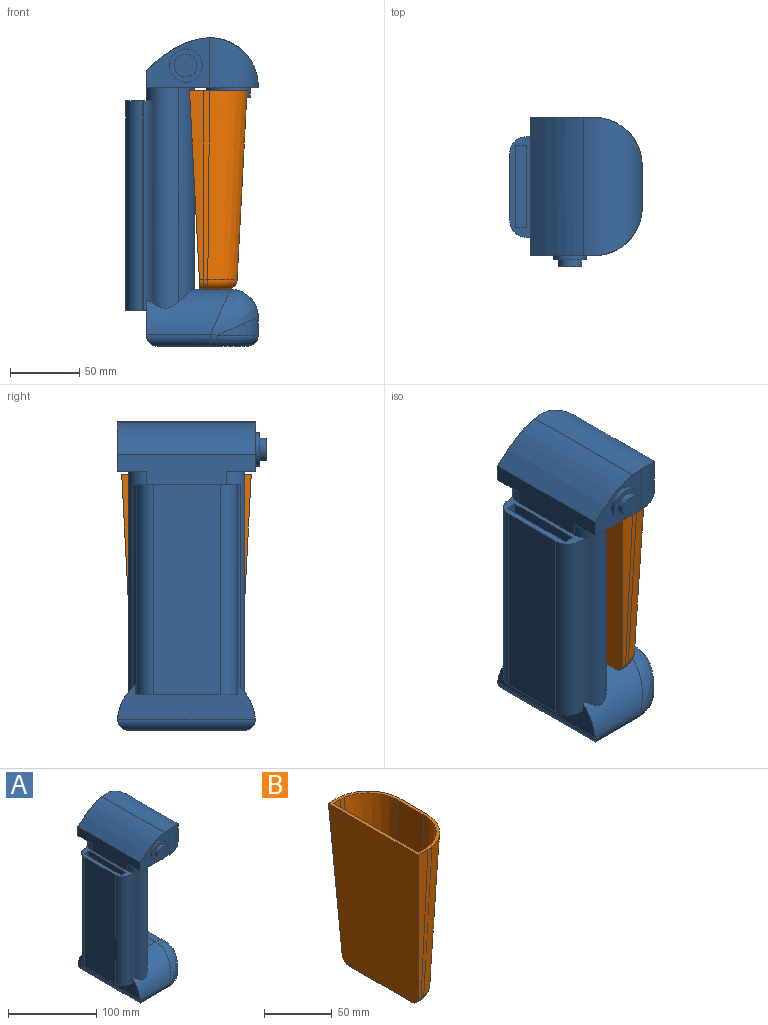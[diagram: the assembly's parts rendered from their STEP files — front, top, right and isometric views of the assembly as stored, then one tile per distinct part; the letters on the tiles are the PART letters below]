
ASSEMBLY  parts=2 mates=1
PART A: 58 faces, bbox 98.9x110.3x223.4 mm
  f0: plane 100.01x22.09mm, normal (-1,0,0), area 1801.5mm2, adj f1,f3,f7,f8,f11,f19,f30,f31
  f1: plane 45.89x36.12mm, normal (0,-1,0), area 830.3mm2, adj f0,f8,f11,f33,f36,f49
  f2: plane 27.57x13.21mm, normal (1,0,0), area 364.2mm2, adj f21,f24,f27,f41
  f3: plane 46.12x36.15mm, normal (0,1,0), area 1284.1mm2, adj f0,f7,f11,f32,f34
  f4: plane 99.68x25.16mm, normal (-1,0,0), area 1748.9mm2, adj f17,f22,f25,f38,f40,f42,f45,f46
  f5: plane 83.68x64.88mm, normal (0,0,-1), area 5096.1mm2, adj f37,f38,f39,f40,f41,f42,f43,f44
  f6: plane 30x1.15mm, normal (1,0,0), area 34.4mm2, adj f11,f32,f33,f34
  f7: extruded ~99.98x38.13mm, area 4502.2mm2, adj f0,f3,f8,f34
  f8: bspline ~44.86x26.77mm, area 1.7mm2, adj f0,f1,f7,f36
  f9: plane 27.57x26.54mm, normal (0,0,1), area 727.4mm2, adj f10,f21,f22,f25,f28,f29
  f10: plane 145.8x20mm, normal (1,0,0), area 2916.1mm2, adj f9,f11,f28,f29
  f11: plane 100x80.88mm, normal (0,0,-1), area 4235.1mm2, adj f0,f1,f3,f6,f10,f12,f28,f29
  f12: cylinder r=16.1mm len=32.2mm, axis (0,0,1), area 687.9mm2, adj f11,f13
  f13: plane 32.2x32.2mm, normal (0,0,-1), area 639.1mm2, adj f12,f14
  f14: cylinder r=7.47mm len=14.93mm, axis (0,0,-1), area 140.8mm2, adj f13,f15
  f15: plane 14.93x14.93mm, normal (0,0,-1), area 175.2mm2, adj f14
  f16: plane 151.61x0.06mm, normal (0,1,0), area 8.7mm2, adj f17,f19,f45,f48
  f17: plane 73.37x15mm, normal (0,0,-1), area 1029.9mm2, adj f4,f16,f18,f20,f45,f46,f47,f48
  f18: plane 151.61x0.52mm, normal (0,-1,0), area 79.4mm2, adj f17,f19,f46,f47
  f19: plane 78.19x20.02mm, normal (0,0,1), area 587.5mm2, adj f0,f16,f18,f20,f30,f31,f45,f46
  f20: plane 151.61x48.74mm, normal (-1,0,0), area 7389.4mm2, adj f17,f19,f47,f48
  f21: cylinder r=20mm len=27.57mm, axis (0,1,0), area 866.3mm2, adj f2,f9,f23,f26
  f22: cylinder r=36.21mm len=60.88mm, axis (-1,0,0), area 2114.3mm2, adj f4,f9,f23,f29,f31,f42,f45
  f23: bspline ~38.03x35.15mm, area 1177.7mm2, adj f21,f22,f24,f44
  f24: cylinder r=36.21mm len=35.59mm, axis (0,0,1), area 331.1mm2, adj f2,f23,f43
  f25: cylinder r=36.21mm len=60.88mm, axis (-1,0,0), area 2113.1mm2, adj f4,f9,f26,f28,f30,f38,f46
  f26: bspline ~38.03x35.15mm, area 1177.6mm2, adj f21,f25,f27,f37
  f27: cylinder r=36.21mm len=35.59mm, axis (0,0,-1), area 331.1mm2, adj f2,f26,f39
  f28: cylinder r=40mm len=155.25mm, axis (0,0,1), area 4646.6mm2, adj f9,f10,f11,f25,f30
  f29: cylinder r=40mm len=155.25mm, axis (0,0,1), area 4646.6mm2, adj f9,f10,f11,f22,f31
  f30: cylinder r=13.4mm len=156.21mm, axis (0,0,1), area 3171.5mm2, adj f0,f11,f19,f25,f28,f46
  f31: cylinder r=13.4mm len=156.02mm, axis (0,0,1), area 3216mm2, adj f0,f11,f19,f22,f29,f45
  f32: cylinder r=35mm len=36.15mm, axis (0,0,1), area 1288mm2, adj f3,f6,f11,f34
  f33: cylinder r=35mm len=36.12mm, axis (0,0,-1), area 1287.2mm2, adj f1,f6,f11,f35
  f34: cylinder r=35mm len=99.98mm, axis (0,-1,0), area 4880.2mm2, adj f3,f6,f7,f32,f35,f36
  f35: bspline ~36.15x35mm, area 0.9mm2, adj f33,f34,f36
  f36: torus R=34.98mm, axis (0,-1,0), area 0.3mm2, adj f1,f8,f34,f35
  f37: bspline ~9.99x9.6mm, area 58.3mm2, adj f5,f26,f38,f39
  f38: cylinder r=8mm len=46.4mm, axis (-1,0,0), area 586.1mm2, adj f4,f5,f25,f37,f40
  f39: torus R=28.21mm, axis (0,0,1), area 579.4mm2, adj f5,f27,f37,f41
  f40: cylinder r=8mm len=99.68mm, axis (0,-1,0), area 1152.1mm2, adj f4,f5,f38,f42
  f41: cylinder r=8mm len=27.57mm, axis (0,1,0), area 346.5mm2, adj f2,f5,f39,f43
  f42: cylinder r=8mm len=46.4mm, axis (-1,0,0), area 586.1mm2, adj f4,f5,f22,f40,f44
  f43: torus R=28.21mm, axis (0,0,1), area 579.4mm2, adj f5,f24,f41,f44
  f44: bspline ~9.97x9.6mm, area 58.3mm2, adj f5,f23,f42,f43
  f45: cylinder r=12mm len=151.61mm, axis (0,0,1), area 1237.9mm2, adj f4,f16,f17,f19,f22,f31
  f46: cylinder r=12mm len=151.61mm, axis (0,0,1), area 1194.6mm2, adj f4,f17,f18,f19,f25,f30
  f47: cylinder r=12mm len=151.61mm, axis (0,0,-1), area 2857.7mm2, adj f17,f18,f19,f20
  f48: cylinder r=12mm len=151.61mm, axis (0,0,1), area 2857.7mm2, adj f16,f17,f19,f20
  f49: cylinder r=12mm len=24mm, axis (0,1,0), area 226.2mm2, adj f1,f50
  f50: plane 24x24mm, normal (0,-1,0), area 238.5mm2, adj f49,f51
  f51: cylinder r=8.25mm len=16.51mm, axis (0,1,0), area 259.3mm2, adj f50,f52
  f52: plane 16.51x16.51mm, normal (0,-1,0), area 214mm2, adj f51
  f53: plane 59.25x20mm, normal (1,0,0), area 1185mm2, adj f19,f54,f56,f57
  f54: plane 20x7.75mm, normal (0,1,0), area 155mm2, adj f19,f53,f55,f57
  f55: plane 59.25x20mm, normal (-1,0,0), area 1185mm2, adj f19,f54,f56,f57
  f56: plane 20x7.75mm, normal (0,-1,0), area 155mm2, adj f19,f53,f55,f57
  f57: plane 59.25x7.75mm, normal (0,0,1), area 459.2mm2, adj f53,f54,f55,f56
PART B: 33 faces, bbox 46.6x98.7x177.3 mm
  f0: plane 136.59x10.13mm, normal (0,-1,-0.05), area 895.5mm2, adj f1,f7,f9,f10
  f1: plane 143.76x93.84mm, normal (-1,0,-0.05), area 12367.8mm2, adj f0,f2,f8,f9,f10,f16
  f2: plane 136.59x10.13mm, normal (0,1,-0.05), area 895.5mm2, adj f1,f3,f9,f16
  f3: bspline ~172.32x9.29mm, area 517.9mm2, adj f2,f4,f9,f15
  f4: cone r=33.21mm half-angle=3deg, axis (0,0,1), area 5611.6mm2, adj f3,f5,f9,f14
  f5: plane 136.59x27.57mm, normal (1,0,-0.05), area 3771.5mm2, adj f4,f6,f9,f13
  f6: cone r=33.21mm half-angle=3deg, axis (0,0,1), area 5611.6mm2, adj f5,f7,f9,f12
  f7: bspline ~172.32x9.29mm, area 517.9mm2, adj f0,f6,f9,f11
  f8: plane 64.59x19.54mm, normal (0,0,-1), area 1118.2mm2, adj f1,f10,f11,f12,f13,f14,f15,f16
  f9: plane 93.68x41.62mm, normal (0,0,1), area 584.4mm2, adj f0,f1,f2,f3,f4,f5,f6,f7
  f10: cylinder r=7.4mm len=7.39mm, axis (-1,0,0), area 31.3mm2, adj f0,f1,f8,f11
  f11: bspline ~7.65x7.01mm, area 29.2mm2, adj f7,f8,f10,f12
  f12: torus R=18.67mm, axis (0,0,-1), area 362mm2, adj f6,f8,f11,f13
  f13: cylinder r=7.4mm len=27.57mm, axis (0,-1,0), area 309.6mm2, adj f5,f8,f12,f14
  f14: torus R=18.67mm, axis (0,0,-1), area 362mm2, adj f4,f8,f13,f15
  f15: bspline ~7.65x7.01mm, area 29.2mm2, adj f3,f8,f14,f16
  f16: cylinder r=7.4mm len=7.39mm, axis (1,0,0), area 31.3mm2, adj f1,f2,f8,f15
  f17: plane 136.46x7.62mm, normal (0,1,0.05), area 553mm2, adj f9,f18,f24,f26
  f18: plane 141.2x88.78mm, normal (1,0,0.05), area 11474.9mm2, adj f9,f17,f19,f25,f26,f32
  f19: plane 136.46x7.62mm, normal (0,-1,0.05), area 553mm2, adj f9,f18,f20,f32
  f20: offset ~177.32x14.29mm, area 453.7mm2, adj f9,f19,f21,f31
  f21: cone r=30.72mm half-angle=3deg, axis (0,0,1), area 5133.2mm2, adj f9,f20,f22,f30
  f22: plane 136.46x27.57mm, normal (-1,0,0.05), area 3767.9mm2, adj f9,f21,f23,f29
  f23: cone r=30.72mm half-angle=3deg, axis (0,0,1), area 5133.2mm2, adj f9,f22,f24,f28
  f24: offset ~177.32x14.29mm, area 453.7mm2, adj f9,f17,f23,f27
  f25: plane 64.59x17.17mm, normal (0,0,1), area 964.9mm2, adj f18,f26,f27,f28,f29,f30,f31,f32
  f26: cylinder r=4.9mm len=4.89mm, axis (-1,0,0), area 2.6mm2, adj f17,f18,f25,f27
  f27: bspline ~5.15x4.64mm, area 17.2mm2, adj f24,f25,f26,f28
  f28: torus R=18.67mm, axis (0,0,-1), area 223.6mm2, adj f23,f25,f27,f29
  f29: cylinder r=4.9mm len=27.57mm, axis (0,-1,0), area 205mm2, adj f22,f25,f28,f30
  f30: torus R=18.67mm, axis (0,0,-1), area 223.6mm2, adj f21,f25,f29,f31
  f31: bspline ~5.15x4.64mm, area 17.2mm2, adj f20,f25,f30,f32
  f32: cylinder r=4.9mm len=4.89mm, axis (1,0,0), area 2.6mm2, adj f18,f19,f25,f31
PLACE A t=(14.23,1.35,-3.36)mm fixed
PLACE B t=(9.1,1.35,-5.56)mm
MATE fastened B.f8 <-> A.f9  axis (0,0,-1) through (21.49,1.35,-78.31)mm
